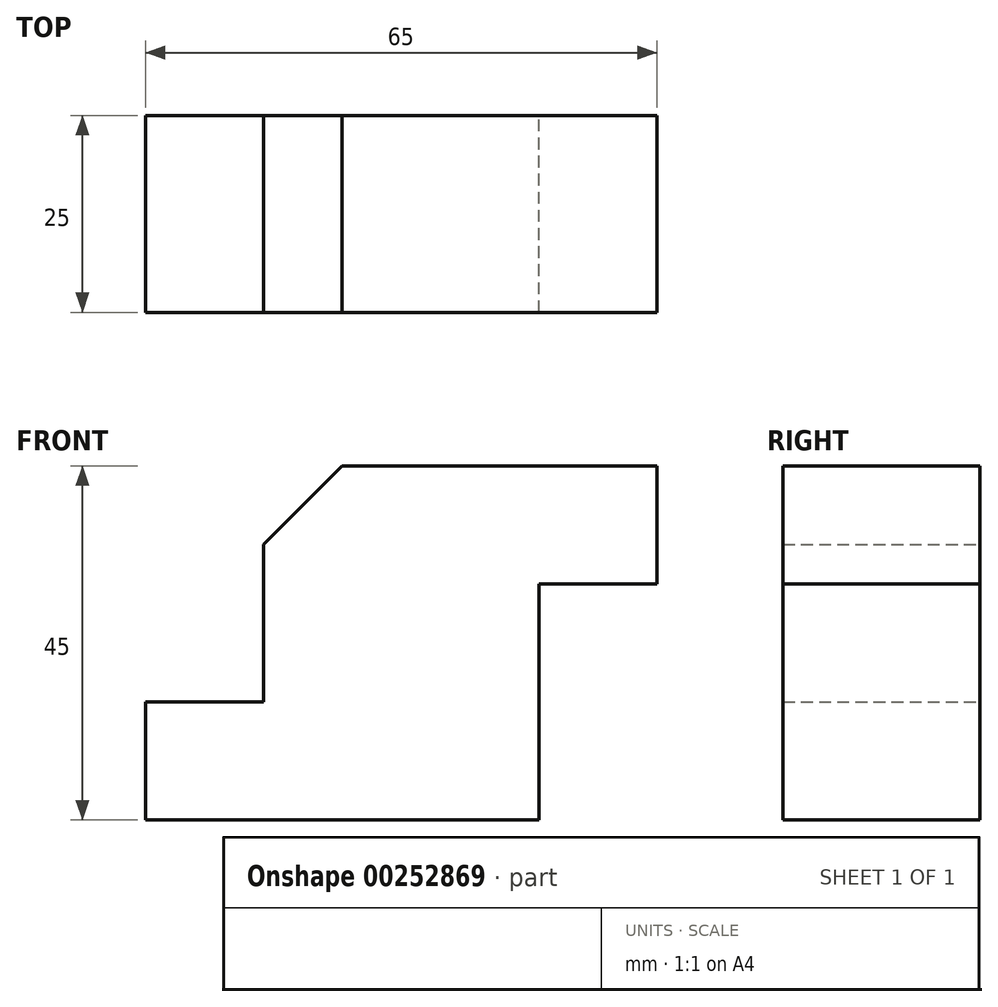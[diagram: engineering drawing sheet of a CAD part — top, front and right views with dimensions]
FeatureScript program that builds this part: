
annotation { "Feature Type Name" : "Feature", "Feature Type Description" : "" }
export const myFeature = defineFeature(function(context is Context, id is Id, definition is map)
    precondition{}
    {
        {
            var Q0;
            Q0=qCreatedBy(makeId("Front.planeOp"),FACE);
            var sketch = newSketch(context, id + "F0", { "sketchPlane" : qUnion([Q0])});
            skLineSegment(sketch, "E0", {"start": v(0, 0) * mm, "end": v(0, 15) * mm});
            skLineSegment(sketch, "E1", {"start": v(0, 15) * mm, "end": v(15, 15) * mm});
            skLineSegment(sketch, "E2", {"start": v(15, 15) * mm, "end": v(15, 45) * mm});
            skLineSegment(sketch, "E3", {"start": v(15, 45) * mm, "end": v(65, 45) * mm});
            skLineSegment(sketch, "E4", {"start": v(65, 45) * mm, "end": v(65, 30) * mm});
            skLineSegment(sketch, "E5", {"start": v(65, 30) * mm, "end": v(50, 30) * mm});
            skLineSegment(sketch, "E6", {"start": v(50, 30) * mm, "end": v(50, 0) * mm});
            skLineSegment(sketch, "E7", {"start": v(50, 0) * mm, "end": v(0, 0) * mm});
            skSolve(sketch);
        }
        {
            var Q0;
            Q0=makeQuery(id+"F0.imprint","IMPRINT",FACE,{"disambiguationData":[TD([[makeQuery(id+"F0.imprint","IMPRINT",EDGE,{"derivedFrom":sQuery(id+"F0.wireOp",EDGE,"E0")}),-1.0]])]});
            extrude(context, id + "F1", {"entities" : qUnion([Q0]), "depth" : 25 * mm, "symmetric" : true});
        }
        {
            var Q0;
            Q0=makeQuery(id+"F1.opExtrude","SWEPT_EDGE",EDGE,{"disambiguationData":[OSD([sQuery(id+"F0.wireOp",EDGE,"E2"),sQuery(id+"F0.wireOp",EDGE,"E3")])]});
            chamfer(context, id + "F2", {"entities" : qUnion([Q0]), "width" : 10 * mm, "tangentPropagation" : true});
        }
    });
